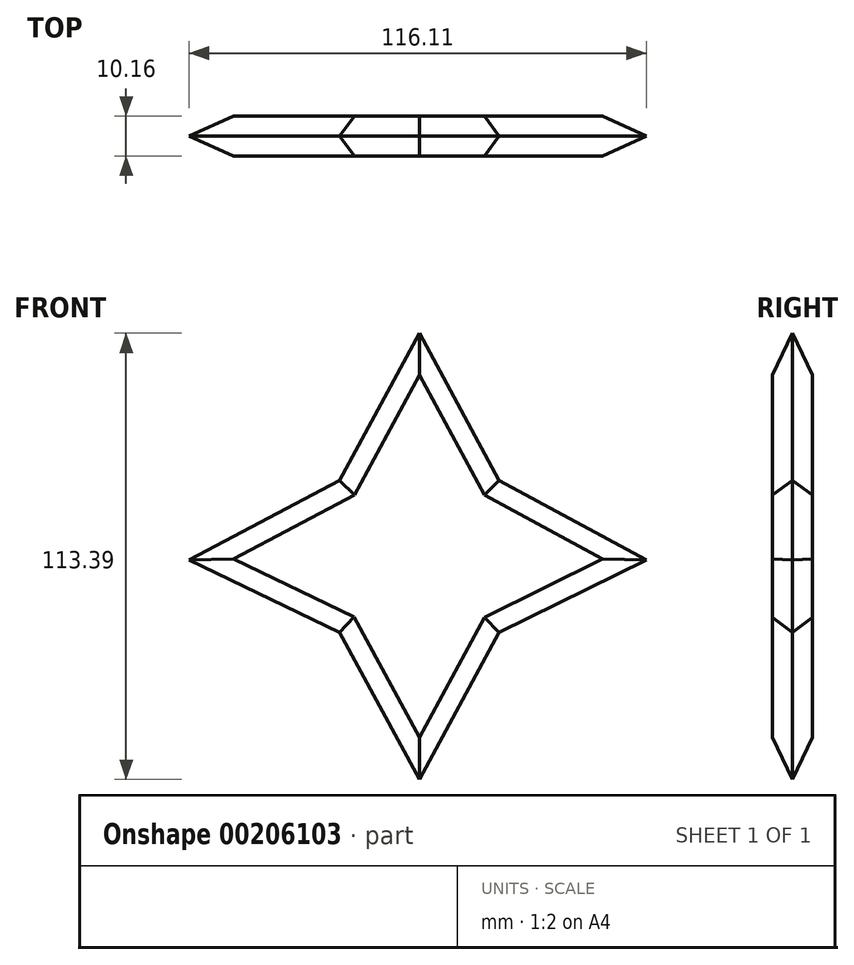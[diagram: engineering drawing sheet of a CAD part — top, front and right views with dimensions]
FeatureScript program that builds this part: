
annotation { "Feature Type Name" : "Feature", "Feature Type Description" : "" }
export const myFeature = defineFeature(function(context is Context, id is Id, definition is map)
    precondition{}
    {
        {
            var Q0;
            Q0=qCreatedBy(makeId("Front.planeOp"),FACE);
            var sketch = newSketch(context, id + "F0", { "sketchPlane" : qUnion([Q0])});
            skPoint(sketch, "E0.end.orphan", {"position": v(-15.12, 49.77) * mm});
            skPoint(sketch, "E1.end.orphan", {"position": v(15.12, 49.77) * mm});
            skPoint(sketch, "E1.start.orphan", {"position": v(0, 76.02) * mm});
            skLineSegment(sketch, "E2", {"start": v(0, 76.02) * mm, "end": v(-20.25, 38.65) * mm});
            skLineSegment(sketch, "E3", {"start": v(0, 76.02) * mm, "end": v(20.25, 38.65) * mm});
            skLineSegment(sketch, "E4", {"start": v(20.25, 38.65) * mm, "end": v(57.64, 18.39) * mm});
            skLineSegment(sketch, "E5", {"start": v(57.64, 18.39) * mm, "end": v(20.25, 0) * mm});
            skLineSegment(sketch, "E6", {"start": v(20.25, 0) * mm, "end": v(0, -37.37) * mm});
            skLineSegment(sketch, "E7", {"start": v(0, -37.37) * mm, "end": v(-20.25, 0) * mm});
            skLineSegment(sketch, "E8", {"start": v(-20.25, 0) * mm, "end": v(-58.47, 18.39) * mm});
            skLineSegment(sketch, "E9", {"start": v(-58.47, 18.39) * mm, "end": v(-20.25, 38.65) * mm});
            skSolve(sketch);
        }
        {
            var Q0;
            Q0 = qSketchRegion(id + "F0", true);
            extrude(context, id + "F1", {"entities" : qUnion([Q0]), "depth" : 10.16 * mm});
        }
        {
            var Q0;
            Q0=makeQuery(id+"F1.opExtrude","CAP_EDGE",EDGE,{"disambiguationData":[OSD([sQuery(id+"F0.wireOp",EDGE,"E9")])],"isStart":false});
            var Q1;
            Q1=makeQuery(id+"F1.opExtrude","CAP_EDGE",EDGE,{"disambiguationData":[OSD([sQuery(id+"F0.wireOp",EDGE,"E2")])],"isStart":false});
            var Q2;
            Q2=makeQuery(id+"F1.opExtrude","CAP_EDGE",EDGE,{"disambiguationData":[OSD([sQuery(id+"F0.wireOp",EDGE,"E3")])],"isStart":false});
            var Q3;
            Q3=makeQuery(id+"F1.opExtrude","CAP_EDGE",EDGE,{"disambiguationData":[OSD([sQuery(id+"F0.wireOp",EDGE,"E4")])],"isStart":false});
            var Q4;
            Q4=makeQuery(id+"F1.opExtrude","CAP_EDGE",EDGE,{"disambiguationData":[OSD([sQuery(id+"F0.wireOp",EDGE,"E5")])],"isStart":false});
            var Q5;
            Q5=makeQuery(id+"F1.opExtrude","CAP_EDGE",EDGE,{"disambiguationData":[OSD([sQuery(id+"F0.wireOp",EDGE,"E6")])],"isStart":false});
            var Q6;
            Q6=makeQuery(id+"F1.opExtrude","CAP_EDGE",EDGE,{"disambiguationData":[OSD([sQuery(id+"F0.wireOp",EDGE,"E7")])],"isStart":false});
            var Q7;
            Q7=makeQuery(id+"F1.opExtrude","CAP_EDGE",EDGE,{"disambiguationData":[OSD([sQuery(id+"F0.wireOp",EDGE,"E8")])],"isStart":false});
            var Q8;
            Q8=makeQuery(id+"F1.opExtrude","CAP_FACE",FACE,{"disambiguationData":[OSD([sQuery(id+"F0.wireOp",EDGE,"E2"),sQuery(id+"F0.wireOp",EDGE,"E3"),sQuery(id+"F0.wireOp",EDGE,"E4"),sQuery(id+"F0.wireOp",EDGE,"E5"),sQuery(id+"F0.wireOp",EDGE,"E6"),sQuery(id+"F0.wireOp",EDGE,"E7"),sQuery(id+"F0.wireOp",EDGE,"E8"),sQuery(id+"F0.wireOp",EDGE,"E9")])],"isStart":true});
            chamfer(context, id + "F2", {"entities" : qUnion([Q0, Q1, Q2, Q3, Q4, Q5, Q6, Q7, Q8]), "width" : 5.08 * mm, "tangentPropagation" : true});
        }
    });
